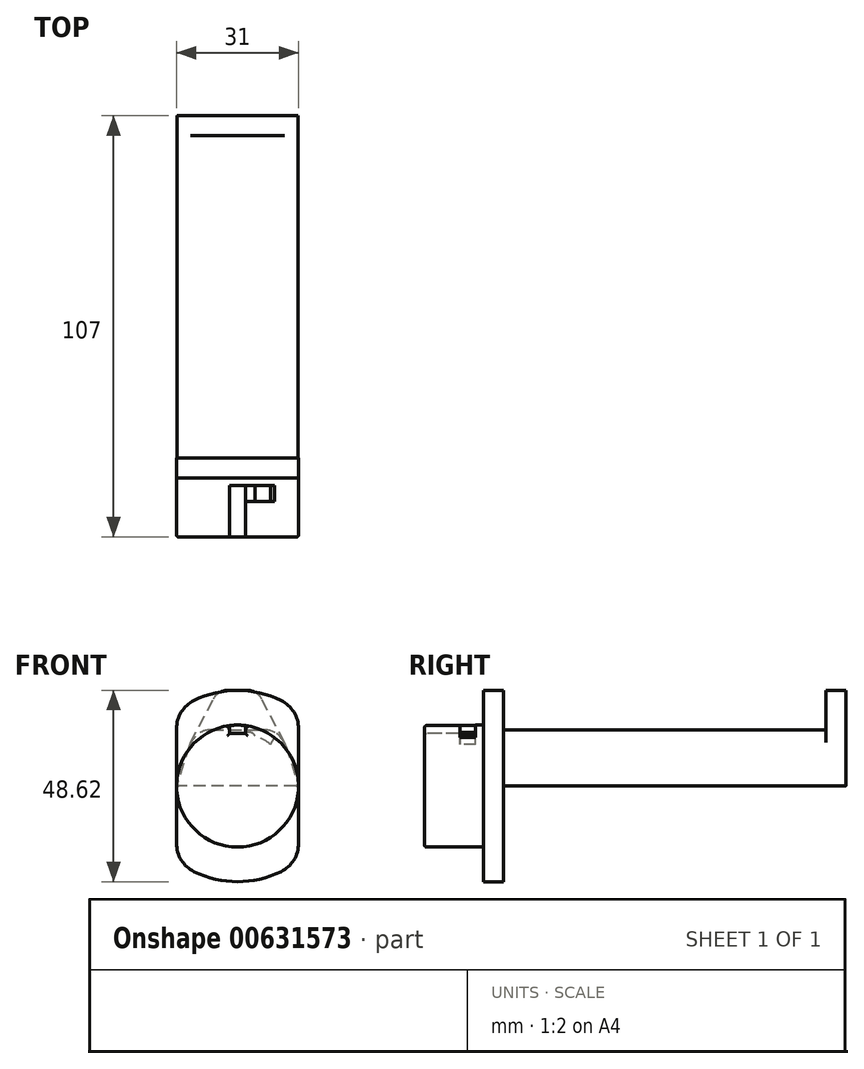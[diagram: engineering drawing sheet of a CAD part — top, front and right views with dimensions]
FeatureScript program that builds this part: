
annotation { "Feature Type Name" : "Feature", "Feature Type Description" : "" }
export const myFeature = defineFeature(function(context is Context, id is Id, definition is map)
    precondition{}
    {
        {
            var Q0;
            Q0=qCreatedBy(makeId("Front.planeOp"),FACE);
            var sketch = newSketch(context, id + "F0", { "sketchPlane" : qUnion([Q0])});
            skCircle(sketch, "E0", {"center": v(0, 0) * mm, "radius": 15.5 * mm});
            skSolve(sketch);
        }
        {
            var Q0;
            Q0 = qSketchRegion(id + "F0", true);
            extrude(context, id + "F1", {"entities" : qUnion([Q0]), "depth" : 15 * mm, "offsetDistance" : 25.4 * mm});
        }
        {
            var Q0;
            Q0=makeQuery(id+"F1.opExtrude","CAP_FACE",FACE,{"disambiguationData":[OSD([sQuery(id+"F0.wireOp",EDGE,"E0")])],"isStart":true});
            var sketch = newSketch(context, id + "F2", { "sketchPlane" : qUnion([Q0])});
            skLineSegment(sketch, "E1", {"start": v(-15.5, 0) * mm, "end": v(15.5, 0) * mm});
            skLineSegment(sketch, "E2", {"start": v(12.32, 10.1) * mm, "end": v(15.5, 0) * mm});
            skPoint(sketch, "E3.visualSharp", {"position": v(11, 14.3) * mm});
            skLineSegment(sketch, "E4", {"start": v(0, 14.3) * mm, "end": v(6.6, 14.3) * mm});
            skLineSegment(sketch, "E5", {"start": v(0, 0) * mm, "end": v(0, 15.5) * mm, "construction": true});
            skPoint(sketch, "E6.MirrorP", {"position": v(-11, 14.3) * mm});
            skLineSegment(sketch, "E7.MirrorCS", {"start": v(0, 14.3) * mm, "end": v(-6.6, 14.3) * mm});
            skLineSegment(sketch, "E8.MirrorCS", {"start": v(-12.32, 10.1) * mm, "end": v(-15.5, 0) * mm});
            skArc(sketch, "E9.filletArc", {"start": v(12.32, 10.1) * mm, "mid": v(10.15, 13.15) * mm, "end": v(6.6, 14.3) * mm});
            skArc(sketch, "E10.filletArc", {"start": v(-6.6, 14.3) * mm, "mid": v(-10.15, 13.15) * mm, "end": v(-12.32, 10.1) * mm});
            skSolve(sketch);
        }
        {
            var Q0;
            {var subQ0=sQuery(id+"F2.wireOp",EDGE,"E10.filletArc");Q0=makeQuery(id+"F2.imprint","IMPRINT",FACE,{"disambiguationData":[TD([[makeQuery(id+"F2.imprint","IMPRINT",EDGE,{"derivedFrom":subQ0}),1.0]])]});}
            var Q1;
            {var subQ6=sQuery(id+"F2.wireOp",EDGE,"E1");Q1=makeQuery(id+"F2.imprint","IMPRINT",FACE,{"disambiguationData":[TD([[makeQuery(id+"F2.imprint","IMPRINT",EDGE,{"derivedFrom":subQ6}),1.0]])]});}
            var Q2;
            {var subQ0=sQuery(id+"F2.wireOp",EDGE,"E9.filletArc");Q2=makeQuery(id+"F2.imprint","IMPRINT",FACE,{"disambiguationData":[TD([[makeQuery(id+"F2.imprint","IMPRINT",EDGE,{"derivedFrom":subQ0}),1.0]])]});}
            extrude(context, id + "F3", {"entities" : qUnion([Q0, Q1, Q2]), "operationType" : NewBodyOperationType.ADD, "depth" : 87 * mm, "offsetDistance" : 25.4 * mm});
        }
        {
            var Q0;
            {var subQ0=sQuery(id+"F2.wireOp",EDGE,"E2");var subQ1=sQuery(id+"F2.wireOp",EDGE,"E1");Q0=makeQuery(id+"F6.boolean.opBoolean","MERGE",EDGE,{"derivedFrom":[makeQuery(id+"F3.opExtrude","SWEPT_EDGE",EDGE,{"disambiguationData":[OSD([sQuery(id+"F0.wireOp",EDGE,"E0"),subQ1,subQ0])]}),makeQuery(id+"F6.opExtrude","SWEPT_EDGE",EDGE,{"disambiguationData":[OSD([subQ1,subQ0])]})]});}
            var Q1;
            {var subQ0=sQuery(id+"F2.wireOp",EDGE,"E8.MirrorCS");var subQ1=sQuery(id+"F2.wireOp",EDGE,"E1");Q1=makeQuery(id+"F6.boolean.opBoolean","MERGE",EDGE,{"derivedFrom":[makeQuery(id+"F3.opExtrude","SWEPT_EDGE",EDGE,{"disambiguationData":[OSD([sQuery(id+"F0.wireOp",EDGE,"E0"),subQ1,subQ0])]}),makeQuery(id+"F6.opExtrude","SWEPT_EDGE",EDGE,{"disambiguationData":[OSD([subQ1,subQ0])]})]});}
            fillet(context, id + "F4", {"entities" : qUnion([Q0, Q1]), "radius" : .5 * mm, "tangentPropagation" : true, "allowEdgeOverflow" : false});
        }
        {
            var Q0;
            Q0=makeQuery(id+"F3.opExtrude","CAP_FACE",FACE,{"disambiguationData":[OSD([sQuery(id+"F2.wireOp",EDGE,"E1"),sQuery(id+"F2.wireOp",EDGE,"hzJfW0gD-snIa-qfyi-ev6L-n8brZvdEBXHB")])],"isStart":false});
            var sketch = newSketch(context, id + "F5", { "sketchPlane" : qUnion([Q0])});
            skLineSegment(sketch, "E11", {"start": v(0, 24.3) * mm, "end": v(0, 0) * mm, "construction": true});
            skLineSegment(sketch, "E12", {"start": v(11.91, 11.09) * mm, "end": v(6.12, 22.16) * mm});
            skLineSegment(sketch, "E13", {"start": v(0, 24.3) * mm, "end": v(2.58, 24.3) * mm});
            skLineSegment(sketch, "E14.MirrorCS", {"start": v(0, 24.3) * mm, "end": v(-2.58, 24.3) * mm});
            skLineSegment(sketch, "E15.MirrorCS", {"start": v(-11.91, 11.09) * mm, "end": v(-6.12, 22.16) * mm});
            skPoint(sketch, "E16.visualSharp", {"position": v(-5, 24.3) * mm});
            skArc(sketch, "E16.filletArc", {"start": v(-2.58, 24.3) * mm, "mid": v(-4.65, 23.73) * mm, "end": v(-6.12, 22.16) * mm});
            skPoint(sketch, "E17.visualSharp", {"position": v(5, 24.3) * mm});
            skArc(sketch, "E17.filletArc", {"start": v(6.12, 22.16) * mm, "mid": v(4.65, 23.73) * mm, "end": v(2.58, 24.3) * mm});
            skSolve(sketch);
        }
        {
            var Q0;
            {var subQ3=sQuery(id+"F5.wireOp",EDGE,"E12");Q0=makeQuery(id+"F5.imprint","IMPRINT",FACE,{"disambiguationData":[TD([[makeQuery(id+"F5.imprint","IMPRINT",EDGE,{"derivedFrom":subQ3}),1.0]])]});}
            var Q1;
            Q1=makeQuery(id+"F5.imprint","IMPRINT",FACE,{"disambiguationData":[TD([[makeQuery(id+"F5.imprint","IMPRINT",EDGE,{"derivedFrom":makeQuery(id+"F3.opExtrude","CAP_EDGE",EDGE,{"disambiguationData":[OSD([sQuery(id+"F2.wireOp",EDGE,"E1")])],"isStart":false})}),1.0]])]});
            extrude(context, id + "F6", {"entities" : qUnion([Q0, Q1]), "operationType" : NewBodyOperationType.ADD, "depth" : 5 * mm, "offsetDistance" : 25.4 * mm});
        }
        {
            var Q0;
            Q0=makeQuery(id+"F1.opExtrude","CAP_FACE",FACE,{"disambiguationData":[OSD([sQuery(id+"F0.wireOp",EDGE,"E0")])],"isStart":true});
            var sketch = newSketch(context, id + "F7", { "sketchPlane" : qUnion([Q0])});
            skArc(sketch, "E18", {"start": v(11.03, 21.74) * mm, "mid": v(0, 24.3) * mm, "end": v(-11.03, 21.74) * mm});
            skLineSegment(sketch, "E19", {"start": v(-15.5, 0) * mm, "end": v(15.5, 0) * mm, "construction": true});
            skLineSegment(sketch, "E20", {"start": v(0, 15.5) * mm, "end": v(0, -15.5) * mm, "construction": true});
            skLineSegment(sketch, "E21", {"start": v(15.5, 0) * mm, "end": v(15.5, 14.57) * mm});
            skLineSegment(sketch, "E22.MirrorCS", {"start": v(-15.5, 0) * mm, "end": v(-15.5, 14.57) * mm});
            skArc(sketch, "E23.filletArc", {"start": v(15.5, 14.57) * mm, "mid": v(14.3, 18.8) * mm, "end": v(11.03, 21.74) * mm});
            skArc(sketch, "E24.MirrorCS", {"start": v(-15.5, 14.57) * mm, "mid": v(-14.3, 18.8) * mm, "end": v(-11.03, 21.74) * mm});
            skLineSegment(sketch, "E25.MirrorCS", {"start": v(-15.5, 0) * mm, "end": v(-15.5, -14.57) * mm});
            skLineSegment(sketch, "E26.MirrorCS", {"start": v(15.5, 0) * mm, "end": v(15.5, -14.57) * mm});
            skArc(sketch, "E27.MirrorCS", {"start": v(15.5, -14.57) * mm, "mid": v(14.3, -18.8) * mm, "end": v(11.03, -21.74) * mm});
            skArc(sketch, "E28.MirrorCS", {"start": v(11.03, -21.74) * mm, "mid": v(0, -24.3) * mm, "end": v(-11.03, -21.74) * mm});
            skArc(sketch, "E29.MirrorCS", {"start": v(-15.5, -14.57) * mm, "mid": v(-14.3, -18.8) * mm, "end": v(-11.03, -21.74) * mm});
            skSolve(sketch);
        }
        {
            var Q0;
            Q0 = qSketchRegion(id + "F7", true);
            extrude(context, id + "F8", {"entities" : qUnion([Q0]), "operationType" : NewBodyOperationType.ADD, "depth" : 5 * mm, "offsetDistance" : 25.4 * mm});
        }
        {
            var Q0;
            Q0=makeQuery(id+"F1.opExtrude","CAP_FACE",FACE,{"disambiguationData":[OSD([sQuery(id+"F0.wireOp",EDGE,"E0")])],"isStart":false});
            var sketch = newSketch(context, id + "F9", { "sketchPlane" : qUnion([Q0])});
            skLineSegment(sketch, "E30", {"start": v(0, 15.5) * mm, "end": v(0, -15.5) * mm, "construction": true});
            skLineSegment(sketch, "E31", {"start": v(15.5, 0) * mm, "end": v(-15.5, 0) * mm, "construction": true});
            skLineSegment(sketch, "E32", {"start": v(0, 13.37) * mm, "end": v(2, 13.37) * mm});
            skLineSegment(sketch, "E33", {"start": v(2, 13.37) * mm, "end": v(2, 15.37) * mm});
            skLineSegment(sketch, "E34.MirrorCS", {"start": v(0, 13.37) * mm, "end": v(-2, 13.37) * mm});
            skLineSegment(sketch, "E35.MirrorCS", {"start": v(-2, 13.37) * mm, "end": v(-2, 15.37) * mm});
            skLineSegment(sketch, "E36.MirrorCS", {"start": v(-15.5, 0) * mm, "end": v(15.5, 0) * mm, "construction": true});
            skLineSegment(sketch, "E37.1.0", {"start": v(13.37, 0) * mm, "end": v(13.37, 2) * mm});
            skLineSegment(sketch, "E37.1.1", {"start": v(13.37, 0) * mm, "end": v(13.37, -2) * mm});
            skLineSegment(sketch, "E37.1.2", {"start": v(13.37, 0) * mm, "end": v(13.37, -2) * mm});
            skLineSegment(sketch, "E37.1.3", {"start": v(13.37, 0) * mm, "end": v(13.37, 2) * mm});
            skLineSegment(sketch, "E37.1.4", {"start": v(13.37, -2) * mm, "end": v(15.37, -2) * mm});
            skLineSegment(sketch, "E37.1.5", {"start": v(13.37, 0) * mm, "end": v(13.37, 2) * mm});
            skLineSegment(sketch, "E37.1.6", {"start": v(13.37, -2) * mm, "end": v(15.37, -2) * mm});
            skLineSegment(sketch, "E37.1.7", {"start": v(13.37, 2) * mm, "end": v(15.37, 2) * mm});
            skLineSegment(sketch, "E37.1.8", {"start": v(13.37, 2) * mm, "end": v(15.37, 2) * mm});
            skLineSegment(sketch, "E37.1.9", {"start": v(13.37, 2) * mm, "end": v(15.37, 2) * mm});
            skLineSegment(sketch, "E37.2.0", {"start": v(0, -13.37) * mm, "end": v(2, -13.37) * mm});
            skLineSegment(sketch, "E37.2.1", {"start": v(0, -13.37) * mm, "end": v(-2, -13.37) * mm});
            skLineSegment(sketch, "E37.2.2", {"start": v(0, -13.37) * mm, "end": v(-2, -13.37) * mm});
            skLineSegment(sketch, "E37.2.3", {"start": v(0, -13.37) * mm, "end": v(2, -13.37) * mm});
            skLineSegment(sketch, "E37.2.4", {"start": v(-2, -13.37) * mm, "end": v(-2, -15.37) * mm});
            skLineSegment(sketch, "E37.2.5", {"start": v(0, -13.37) * mm, "end": v(2, -13.37) * mm});
            skLineSegment(sketch, "E37.2.6", {"start": v(-2, -13.37) * mm, "end": v(-2, -15.37) * mm});
            skLineSegment(sketch, "E37.2.7", {"start": v(2, -13.37) * mm, "end": v(2, -15.37) * mm});
            skLineSegment(sketch, "E37.2.8", {"start": v(2, -13.37) * mm, "end": v(2, -15.37) * mm});
            skLineSegment(sketch, "E37.2.9", {"start": v(2, -13.37) * mm, "end": v(2, -15.37) * mm});
            skLineSegment(sketch, "E37.3.0", {"start": v(-13.37, 0) * mm, "end": v(-13.37, -2) * mm});
            skLineSegment(sketch, "E37.3.1", {"start": v(-13.37, 0) * mm, "end": v(-13.37, 2) * mm});
            skLineSegment(sketch, "E37.3.2", {"start": v(-13.37, 0) * mm, "end": v(-13.37, 2) * mm});
            skLineSegment(sketch, "E37.3.3", {"start": v(-13.37, 0) * mm, "end": v(-13.37, -2) * mm});
            skLineSegment(sketch, "E37.3.4", {"start": v(-13.37, 2) * mm, "end": v(-15.37, 2) * mm});
            skLineSegment(sketch, "E37.3.5", {"start": v(-13.37, 0) * mm, "end": v(-13.37, -2) * mm});
            skLineSegment(sketch, "E37.3.6", {"start": v(-13.37, 2) * mm, "end": v(-15.37, 2) * mm});
            skLineSegment(sketch, "E37.3.7", {"start": v(-13.37, -2) * mm, "end": v(-15.37, -2) * mm});
            skLineSegment(sketch, "E37.3.8", {"start": v(-13.37, -2) * mm, "end": v(-15.37, -2) * mm});
            skLineSegment(sketch, "E37.3.9", {"start": v(-13.37, -2) * mm, "end": v(-15.37, -2) * mm});
            skPoint(sketch, "E37.center", {"position": v(0, 0) * mm});
            skLineSegment(sketch, "E37.anchor1", {"start": v(0, 0) * mm, "end": v(-2, 13.37) * mm, "construction": true});
            skLineSegment(sketch, "E37.anchor2", {"start": v(0, 0) * mm, "end": v(-13.37, -2) * mm, "construction": true});
            skSolve(sketch);
        }
        {
            var Q0;
            {var subQ1=sQuery(id+"F9.wireOp",EDGE,"E33");Q0=makeQuery(id+"F9.imprint","IMPRINT",FACE,{"disambiguationData":[TD([[makeQuery(id+"F9.imprint","IMPRINT",EDGE,{"derivedFrom":subQ1}),1.0]])]});}
            var Q1;
            Q1=makeQuery(id+"F9.imprint","IMPRINT",FACE,{"disambiguationData":[TD([[makeQuery(id+"F9.imprint","IMPRINT",EDGE,{"derivedFrom":sQuery(id+"F9.wireOp",EDGE,"E37.1.2")}),1.0]])]});
            var Q2;
            Q2=makeQuery(id+"F9.imprint","IMPRINT",FACE,{"disambiguationData":[TD([[makeQuery(id+"F9.imprint","IMPRINT",EDGE,{"derivedFrom":sQuery(id+"F9.wireOp",EDGE,"E37.2.2")}),1.0]])]});
            var Q3;
            Q3=makeQuery(id+"F9.imprint","IMPRINT",FACE,{"disambiguationData":[TD([[makeQuery(id+"F9.imprint","IMPRINT",EDGE,{"derivedFrom":sQuery(id+"F9.wireOp",EDGE,"E37.3.2")}),1.0]])]});
            var Q4;
            Q4=makeQuery(id+"F8.opExtrude","CAP_FACE",FACE,{"disambiguationData":[OSD([sQuery(id+"F7.wireOp",EDGE,"E18"),sQuery(id+"F7.wireOp",EDGE,"ctbfgFI7-FcDD-Jrus-rc5D-pnfEDY36C1dK"),sQuery(id+"F7.wireOp",EDGE,"6ffd2a1d-91c1-4a17-a6e3-66ea29e1914e0.MirrorCS"),sQuery(id+"F7.wireOp",EDGE,"3b9ce4da-b91f-49c3-af16-0c7b2ce4fa6a.trimOffspring"),sQuery(id+"F7.wireOp",EDGE,"8cc4f46d-6b77-47f0-aa44-f1b52df85da2.filletArc"),sQuery(id+"F7.wireOp",EDGE,"53c5d7b3-cc1b-4d80-99ce-fd1a14b0ec74.filletArc"),sQuery(id+"F7.wireOp",EDGE,"df3cf315-5265-4bc0-986c-5bf307714888.filletArc"),sQuery(id+"F7.wireOp",EDGE,"fb394436-cc09-4701-ac78-3c4c505cba63.filletArc")])],"isStart":true});
            extrude(context, id + "F10", {"entities" : qUnion([Q0, Q1, Q2, Q3]), "operationType" : NewBodyOperationType.REMOVE, "endBound" : BoundingType.UP_TO_SURFACE, "oppositeDirection" : true, "depth" : 7.77 * mm, "endBoundEntityFace" : qUnion([Q4]), "hasOffset" : true, "offsetDistance" : 2 * mm});
        }
        {
            var Q0;
            Q0=makeQuery(id+"F10.boolean.opBoolean","COPY",FACE,{"derivedFrom":makeQuery(id+"F10.opExtrude","SWEPT_FACE",FACE,{"disambiguationData":[OSD([sQuery(id+"F9.wireOp",EDGE,"E33")])]})});
            var sketch = newSketch(context, id + "F11", { "sketchPlane" : qUnion([Q0])});
            skLineSegment(sketch, "E38.bottom", {"start": v(2, 15.37) * mm, "end": v(6, 15.37) * mm});
            skLineSegment(sketch, "E38.top", {"start": v(2, 13.37) * mm, "end": v(6, 13.37) * mm});
            skLineSegment(sketch, "E38.left", {"start": v(2, 15.37) * mm, "end": v(2, 13.37) * mm});
            skLineSegment(sketch, "E38.right", {"start": v(6, 15.37) * mm, "end": v(6, 13.37) * mm});
            skSolve(sketch);
        }
        {
            var Q0;
            Q0=makeQuery(id+"F11.imprint","IMPRINT",FACE,{"disambiguationData":[TD([[makeQuery(id+"F11.imprint","IMPRINT",EDGE,{"derivedFrom":sQuery(id+"F11.wireOp",EDGE,"E38.bottom")}),-1.0]])]});
            var Q1;
            Q1=makeQuery(id+"F1.opExtrude","SWEPT_FACE",FACE,{"disambiguationData":[OSD([sQuery(id+"F0.wireOp",EDGE,"E0")])]});
            revolve(context, id + "F12", {"operationType" : NewBodyOperationType.REMOVE, "entities" : qUnion([Q0]), "axis" : qUnion([Q1]), "revolveType" : RevolveType.ONE_DIRECTION, "angle" : 30 * degree});
        }
        {
            var Q0;
            Q0=makeQuery(id+"F12.boolean.opBoolean","COPY",FACE,{"derivedFrom":makeQuery(id+"F12.opRevolve","SWEPT_FACE",FACE,{"disambiguationData":[OSD([sQuery(id+"F11.wireOp",EDGE,"E38.right")])]})});
            var sketch = newSketch(context, id + "F13", { "sketchPlane" : qUnion([Q0])});
            skArc(sketch, "E39", {"start": v(-2, 13.37) * mm, "mid": v(-3.34, 13.62) * mm, "end": v(-4.42, 12.78) * mm});
            skSolve(sketch);
        }
        {
            var Q0;
            {var subQ0=sQuery(id+"F13.wireOp",EDGE,"E39");Q0=makeQuery(id+"F13.imprint","IMPRINT",FACE,{"disambiguationData":[TD([[makeQuery(id+"F13.imprint","IMPRINT",EDGE,{"derivedFrom":subQ0}),1.0]])]});}
            extrude(context, id + "F14", {"entities" : qUnion([Q0]), "operationType" : NewBodyOperationType.ADD, "endBound" : BoundingType.UP_TO_NEXT, "depth" : 25 * mm, "offsetDistance" : 25 * mm});
        }
        {
            var Q0;
            Q0=makeQuery(id+"F1.opExtrude","CAP_FACE",FACE,{"disambiguationData":[OSD([sQuery(id+"F0.wireOp",EDGE,"E0")])],"isStart":false});
            fillet(context, id + "F15", {"entities" : qUnion([Q0]), "radius" : .5 * mm, "tangentPropagation" : true, "allowEdgeOverflow" : false});
        }
    });
